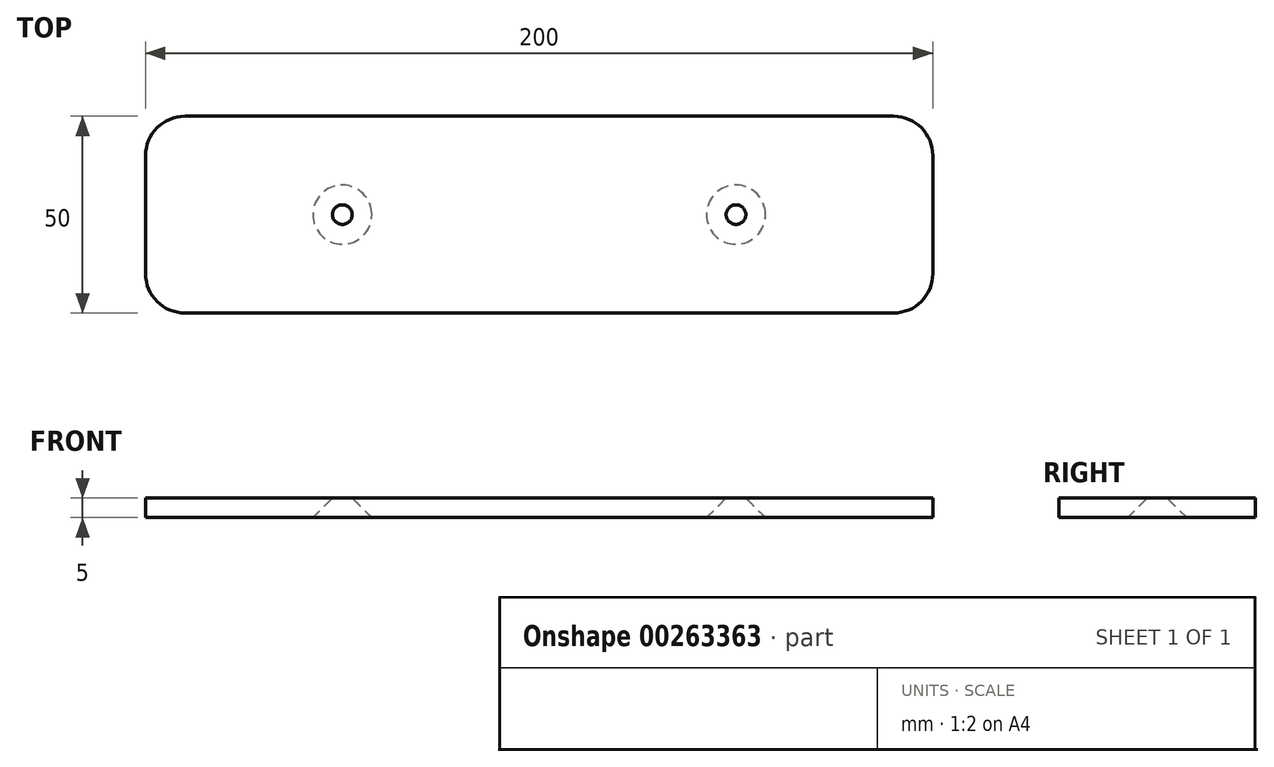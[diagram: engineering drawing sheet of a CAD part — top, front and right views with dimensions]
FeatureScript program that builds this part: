
annotation { "Feature Type Name" : "Feature", "Feature Type Description" : "" }
export const myFeature = defineFeature(function(context is Context, id is Id, definition is map)
    precondition{}
    {
        {
            var Q0;
            Q0=qCreatedBy(makeId("Top.planeOp"),FACE);
            var sketch = newSketch(context, id + "F0", { "sketchPlane" : qUnion([Q0])});
            skLineSegment(sketch, "E0.bottom", {"start": v(90, 25) * mm, "end": v(-90, 25) * mm});
            skLineSegment(sketch, "E0.top", {"start": v(90, -25) * mm, "end": v(-90, -25) * mm});
            skLineSegment(sketch, "E0.left", {"start": v(100, 15) * mm, "end": v(100, -15) * mm});
            skLineSegment(sketch, "E0.right", {"start": v(-100, 15) * mm, "end": v(-100, -15) * mm});
            skPoint(sketch, "E0.middle", {"position": v(0, 0) * mm});
            skCircle(sketch, "E1", {"center": v(-50, 0) * mm, "radius": 2.5 * mm});
            skCircle(sketch, "E2", {"center": v(50, 0) * mm, "radius": 2.5 * mm});
            skPoint(sketch, "E3.visualSharp", {"position": v(100, 25) * mm});
            skArc(sketch, "E3.filletArc", {"start": v(100, 15) * mm, "mid": v(97.07, 22.07) * mm, "end": v(90, 25) * mm});
            skPoint(sketch, "E4.visualSharp", {"position": v(100, -25) * mm});
            skArc(sketch, "E4.filletArc", {"start": v(90, -25) * mm, "mid": v(97.07, -22.07) * mm, "end": v(100, -15) * mm});
            skPoint(sketch, "E5.visualSharp", {"position": v(-100, 25) * mm});
            skArc(sketch, "E5.filletArc", {"start": v(-90, 25) * mm, "mid": v(-97.07, 22.07) * mm, "end": v(-100, 15) * mm});
            skPoint(sketch, "E6.visualSharp", {"position": v(-100, -25) * mm});
            skArc(sketch, "E6.filletArc", {"start": v(-100, -15) * mm, "mid": v(-97.07, -22.07) * mm, "end": v(-90, -25) * mm});
            skSolve(sketch);
        }
        {
            var Q0;
            Q0=makeQuery(id+"F0.imprint","IMPRINT",FACE,{"disambiguationData":[TD([[makeQuery(id+"F0.imprint","IMPRINT",EDGE,{"derivedFrom":sQuery(id+"F0.wireOp",EDGE,"E0.bottom")}),1.0]])]});
            extrude(context, id + "F1", {"entities" : qUnion([Q0]), "depth" : 5 * mm});
        }
        {
            var Q0;
            Q0=makeQuery(id+"F1.opExtrude","CAP_EDGE",EDGE,{"disambiguationData":[OSD([sQuery(id+"F0.wireOp",EDGE,"E1")])],"isStart":true});
            var Q1;
            Q1=makeQuery(id+"F1.opExtrude","CAP_EDGE",EDGE,{"disambiguationData":[OSD([sQuery(id+"F0.wireOp",EDGE,"E2")])],"isStart":true});
            chamfer(context, id + "F2", {"entities" : qUnion([Q0, Q1]), "width" : 5 * mm, "tangentPropagation" : true});
        }
    });
